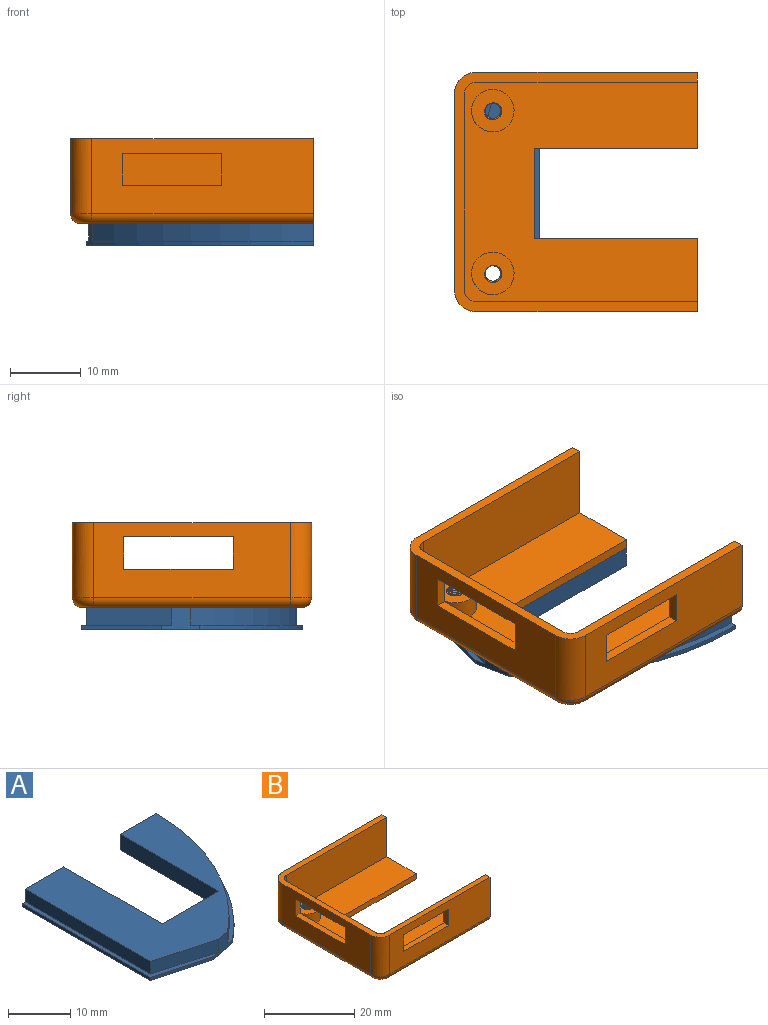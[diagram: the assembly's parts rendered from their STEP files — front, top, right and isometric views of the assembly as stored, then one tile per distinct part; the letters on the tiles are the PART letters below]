
ASSEMBLY  parts=2 mates=1
PART A: 18 faces, bbox 31.3x32.1x3.1 mm
  f0: plane 12.83x3.1mm, normal (0,1,0), area 39.8mm2, adj f10,f11,f12,f17
  f1: plane 12.05x3.32mm, normal (-0.27,-0.96,0), area 31.2mm2, adj f4,f8,f14,f17
  f2: plane 11.28x3.02mm, normal (-0.26,-0.97,0), area 7mm2, adj f4,f8,f9,f10
  f3: cylinder r=38.76mm len=30.92mm, axis (0,0,-1), area 21.2mm2, adj f4,f6,f7,f10
  f4: plane 5.49x3.1mm, normal (0.2,-0.98,0), area 10.1mm2, adj f1,f2,f3,f5,f6,f8,f10,f17
  f5: cylinder r=40.72mm len=31.19mm, axis (0,0,-1), area 89.4mm2, adj f4,f6,f13,f17
  f6: plane 31.22x15.88mm, normal (0,0,1), area 33mm2, adj f3,f4,f5,f7,f13,f15
  f7: cylinder r=38.76mm len=0.6mm, axis (0,0,-1), area 0mm2, adj f3,f6,f10,f15
  f8: plane 32.05x12.77mm, normal (0,0,1), area 29.4mm2, adj f1,f2,f4,f9,f14,f16
  f9: plane 29.03x0.6mm, normal (-1,0,0), area 17.4mm2, adj f2,f8,f10,f16
  f10: plane 32.05x31.28mm, normal (0,0,-1), area 546.3mm2, adj f0,f2,f3,f4,f7,f9,f11,f12
  f11: plane 22.37x3.1mm, normal (-1,0,0), area 69.3mm2, adj f0,f10,f15,f17
  f12: plane 22.37x3.1mm, normal (1,0,0), area 69.3mm2, adj f0,f10,f16,f17
  f13: cylinder r=40.72mm len=2.5mm, axis (0,0,-1), area 0.1mm2, adj f5,f6,f15,f17
  f14: plane 28.43x2.5mm, normal (-1,0,0), area 71.1mm2, adj f1,f8,f16,f17
  f15: plane 9.01x3.1mm, normal (0,1,0), area 25.9mm2, adj f6,f7,f10,f11,f13,f17
  f16: plane 9.44x3.1mm, normal (0,1,0), area 27.5mm2, adj f8,f9,f10,f12,f14,f17
  f17: plane 31.75x29.74mm, normal (0,0,1), area 483.9mm2, adj f0,f1,f4,f5,f11,f12,f13,f14
PART B: 47 faces, bbox 34.6x34.4x12.1 mm
  f0: plane 12x10.28mm, normal (1,0,0), area 28.8mm2, adj f1,f2,f37,f39,f40,f42,f45
  f1: plane 32.9x31mm, normal (0,0,1), area 668mm2, adj f0,f3,f32,f33,f34,f35,f36,f37
  f2: plane 32.9x31mm, normal (0,0,-1), area 685.3mm2, adj f0,f3,f27,f28,f29,f30,f31,f40
  f3: plane 12x10.73mm, normal (1,0,0), area 29.4mm2, adj f1,f2,f38,f39,f41,f43,f46
  f4: bspline ~3.21x2.57mm, area 14.6mm2, adj f5,f12,f13,f18
  f5: cylinder r=1.28mm len=2.99mm, axis (0,0,-1), area 5.3mm2, adj f4,f6,f13,f18
  f6: bspline ~3.21x2.56mm, area 14.6mm2, adj f5,f12,f13,f18,f31
  f7: bspline ~3.21x2.57mm, area 14.6mm2, adj f8,f10,f11,f19
  f8: cylinder r=1.28mm len=2.99mm, axis (0,0,-1), area 5.3mm2, adj f7,f9,f11,f19
  f9: bspline ~3.21x2.56mm, area 14.6mm2, adj f8,f10,f11,f19,f30
  f10: cylinder r=1.09mm len=2.99mm, axis (0,0,1), area 2.5mm2, adj f7,f9,f19,f30
  f11: plane 2.51x2.48mm, normal (0,0,1), area 0.8mm2, adj f7,f8,f9,f30
  f12: cylinder r=1.09mm len=2.99mm, axis (0,0,1), area 2.5mm2, adj f4,f6,f18,f31
  f13: plane 2.51x2.48mm, normal (0,0,1), area 0.8mm2, adj f4,f5,f6,f31
  f14: plane 15.5x1.4mm, normal (0,0,-1), area 21.7mm2, adj f15,f17,f21,f33
  f15: plane 4.6x1.4mm, normal (0,1,0), area 6.4mm2, adj f14,f16,f21,f33
  f16: plane 15.5x1.4mm, normal (0,0,1), area 21.7mm2, adj f15,f17,f21,f33
  f17: plane 4.6x1.4mm, normal (0,-1,0), area 6.4mm2, adj f14,f16,f21,f33
  f18: plane 6.1x6.1mm, normal (0,0,1), area 23.8mm2, adj f4,f5,f6,f12,f35
  f19: plane 6.1x6.1mm, normal (0,0,1), area 23.8mm2, adj f7,f8,f9,f10,f36
  f20: cylinder r=3mm len=10.6mm, axis (0,0,1), area 50mm2, adj f21,f29,f39,f42
  f21: plane 27.8x10.6mm, normal (-1,0,0), area 223.4mm2, adj f14,f15,f16,f17,f20,f22,f28,f39
  f22: cylinder r=3mm len=10.6mm, axis (0,0,1), area 50mm2, adj f21,f27,f39,f43
  f23: plane 4.5x1.4mm, normal (-1,0,0), area 6.3mm2, adj f24,f26,f37,f42
  f24: plane 14x1.4mm, normal (0,0,1), area 19.6mm2, adj f23,f25,f37,f42
  f25: plane 4.5x1.4mm, normal (1,0,0), area 6.3mm2, adj f24,f26,f37,f42
  f26: plane 14x1.4mm, normal (0,0,-1), area 19.6mm2, adj f23,f25,f37,f42
  f27: torus R=1.6mm, axis (0,0,1), area 8.6mm2, adj f2,f22,f28,f41
  f28: cylinder r=1.4mm len=27.8mm, axis (0,1,0), area 61.1mm2, adj f2,f21,f27,f29
  f29: torus R=1.6mm, axis (0,0,1), area 8.6mm2, adj f2,f20,f28,f40
  f30: cone r=1.88mm half-angle=45deg, axis (0,0,-1), area 22.5mm2, adj f2,f9,f10,f11
  f31: cone r=1.88mm half-angle=45deg, axis (0,0,-1), area 22.5mm2, adj f2,f6,f12,f13
  f32: cylinder r=1.6mm len=10.6mm, axis (0,0,1), area 26.6mm2, adj f1,f33,f37,f39
  f33: plane 27.8x10.6mm, normal (1,0,0), area 223.4mm2, adj f1,f14,f15,f16,f17,f32,f34,f39
  f34: cylinder r=1.6mm len=10.6mm, axis (0,0,1), area 26.6mm2, adj f1,f33,f38,f39
  f35: cylinder r=3mm len=6mm, axis (0,0,1), area 56.5mm2, adj f1,f18
  f36: cylinder r=3mm len=6mm, axis (0,0,1), area 56.5mm2, adj f1,f19
  f37: plane 31.3x10.6mm, normal (0,1,0), area 268.8mm2, adj f0,f1,f23,f24,f25,f26,f32,f39
  f38: plane 31.3x10.6mm, normal (0,-1,0), area 331.8mm2, adj f1,f3,f34,f39
  f39: plane 34.3x33.8mm, normal (0,0,1), area 136.7mm2, adj f0,f3,f20,f21,f22,f32,f33,f34
  f40: cylinder r=1.4mm len=31.3mm, axis (-1,0,0), area 68.8mm2, adj f0,f2,f29,f42
  f41: cylinder r=1.4mm len=31.3mm, axis (1,0,0), area 68.8mm2, adj f2,f3,f27,f43
  f42: plane 31.3x10.6mm, normal (0,-1,0), area 268.8mm2, adj f0,f20,f23,f24,f25,f26,f39,f40
  f43: plane 31.3x10.6mm, normal (0,1,0), area 331.8mm2, adj f3,f22,f39,f41
  f44: plane 12.79x1.4mm, normal (1,0,0), area 17.9mm2, adj f1,f2,f45,f46
  f45: plane 23x1.4mm, normal (0,1,0), area 32.2mm2, adj f0,f1,f2,f44
  f46: plane 23x1.4mm, normal (0,-1,0), area 32.2mm2, adj f1,f2,f3,f44
PLACE A rot(axis=(0,0,-1),90deg) t=(32.4,-15.21,-3.1)mm
PLACE B at identity
MATE fastened A.f15 <-> B.f0  axis (1,0,0) through (32.4,-21.63,0)mm
